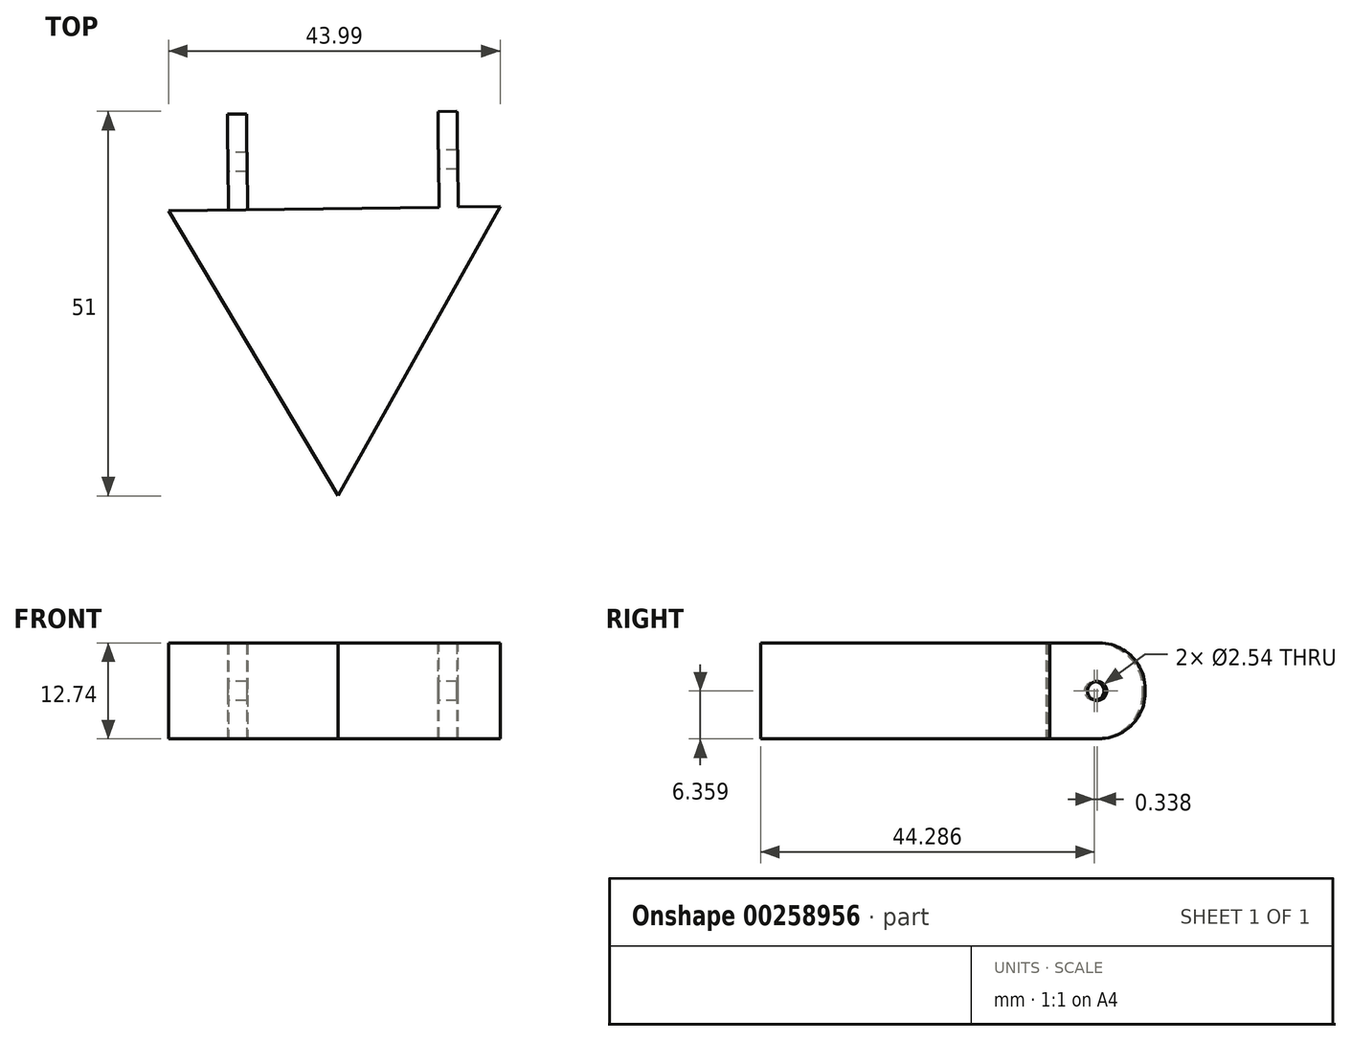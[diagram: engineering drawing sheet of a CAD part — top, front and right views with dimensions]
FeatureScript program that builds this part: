
annotation { "Feature Type Name" : "Feature", "Feature Type Description" : "" }
export const myFeature = defineFeature(function(context is Context, id is Id, definition is map)
    precondition{}
    {
        {
            var Q0;
            Q0=qCreatedBy(makeId("Top.planeOp"),FACE);
            var sketch = newSketch(context, id + "F0", { "sketchPlane" : qUnion([Q0])});
            skCircle(sketch, "E0.cCircle", {"center": v(0, 0) * mm, "radius": 12.7 * mm, "construction": true});
            skLineSegment(sketch, "E0.0", {"start": v(-25, 4.47) * mm, "end": v(16.38, 19.42) * mm});
            skLineSegment(sketch, "E0.1", {"start": v(16.38, 19.42) * mm, "end": v(8.63, -23.9) * mm});
            skLineSegment(sketch, "E0.2", {"start": v(8.63, -23.9) * mm, "end": v(-25, 4.47) * mm});
            skPoint(sketch, "E0.0.midPoint", {"position": v(-4.31, 11.95) * mm});
            skSolve(sketch);
        }
        {
            var Q0;
            Q0=makeQuery(id+"F0.imprint","IMPRINT",FACE,{"disambiguationData":[TD([[makeQuery(id+"F0.imprint","IMPRINT",EDGE,{"derivedFrom":sQuery(id+"F0.wireOp",EDGE,"E0.0")}),-1.0]])]});
            extrude(context, id + "F1", {"entities" : qUnion([Q0]), "depth" : 12.7 * mm});
        }
        {
            var Q0;
            Q0=makeQuery(id+"F1.opExtrude","SWEPT_BODY",BODY,{"disambiguationData":[OSD([sQuery(id+"F0.wireOp",EDGE,"E0.0"),sQuery(id+"F0.wireOp",EDGE,"E0.1"),sQuery(id+"F0.wireOp",EDGE,"E0.2")])]});
            deleteBodies(context, id + "F2", {"entities" : qUnion([Q0])});
        }
        {
            var Q0;
            Q0=qCreatedBy(makeId("Top.planeOp"),FACE);
            var sketch = newSketch(context, id + "F3", { "sketchPlane" : qUnion([Q0])});
            skCircle(sketch, "E1.cCircle", {"center": v(0, 0) * mm, "radius": 12.7 * mm, "construction": true});
            skLineSegment(sketch, "E1.0", {"start": v(21.84, 12.97) * mm, "end": v(0.3, -25.4) * mm});
            skLineSegment(sketch, "E1.1", {"start": v(0.3, -25.4) * mm, "end": v(-22.15, 12.43) * mm});
            skLineSegment(sketch, "E1.2", {"start": v(-22.15, 12.43) * mm, "end": v(21.84, 12.97) * mm});
            skPoint(sketch, "E1.0.midPoint", {"position": v(11.07, -6.22) * mm});
            skSolve(sketch);
        }
        {
            var Q0;
            Q0=makeQuery(id+"F3.imprint","IMPRINT",FACE,{"disambiguationData":[TD([[makeQuery(id+"F3.imprint","IMPRINT",EDGE,{"derivedFrom":sQuery(id+"F3.wireOp",EDGE,"E1.0")}),-1.0]])]});
            extrude(context, id + "F4", {"entities" : qUnion([Q0]), "depth" : 12.7 * mm});
        }
        {
            var Q0;
            Q0=makeQuery(id+"F4.opExtrude","SWEPT_FACE",FACE,{"disambiguationData":[OSD([sQuery(id+"F3.wireOp",EDGE,"E1.2")])]});
            var sketch = newSketch(context, id + "F5", { "sketchPlane" : qUnion([Q0])});
            skLineSegment(sketch, "E2.bottom", {"start": v(-13.88, 0) * mm, "end": v(-16.42, 0) * mm});
            skLineSegment(sketch, "E2.top", {"start": v(-13.88, 12.7) * mm, "end": v(-16.42, 12.7) * mm});
            skLineSegment(sketch, "E2.left", {"start": v(-13.88, 0) * mm, "end": v(-13.88, 12.7) * mm});
            skLineSegment(sketch, "E2.right", {"start": v(-16.42, 0) * mm, "end": v(-16.42, 12.7) * mm});
            skPoint(sketch, "E3.end.orphan", {"position": v(-1.18, 0) * mm});
            skPoint(sketch, "E3.start.orphan", {"position": v(-1.18, 12.7) * mm});
            skPoint(sketch, "E4.orphan", {"position": v(-2.45, 12.7) * mm});
            skPoint(sketch, "E5.top.start.orphan", {"position": v(0.09, 12.7) * mm});
            skPoint(sketch, "E6.orphan", {"position": v(-2.45, 0) * mm});
            skPoint(sketch, "E5.bottom.start.orphan", {"position": v(0.09, 0) * mm});
            skLineSegment(sketch, "E7.bottom", {"start": v(11.52, 12.66) * mm, "end": v(14.06, 12.66) * mm});
            skLineSegment(sketch, "E7.top", {"start": v(11.52, -0.04) * mm, "end": v(14.06, -0.04) * mm});
            skLineSegment(sketch, "E7.left", {"start": v(11.52, 12.66) * mm, "end": v(11.52, -0.04) * mm});
            skLineSegment(sketch, "E7.right", {"start": v(14.06, 12.66) * mm, "end": v(14.06, -0.04) * mm});
            skLineSegment(sketch, "E8", {"start": v(-1.18, 12.7) * mm, "end": v(-1.18, 0) * mm, "construction": true});
            skSolve(sketch);
        }
        {
            var Q0;
            Q0 = qSketchRegion(id + "F5", true);
            extrude(context, id + "F6", {"entities" : qUnion([Q0]), "operationType" : NewBodyOperationType.ADD, "depth" : 12.7 * mm});
        }
        {
            var Q0;
            Q0=makeQuery(id+"F6.opExtrude","SWEPT_FACE",FACE,{"disambiguationData":[OSD([sQuery(id+"F5.wireOp",EDGE,"E7.right")])]});
            var sketch = newSketch(context, id + "F7", { "sketchPlane" : qUnion([Q0])});
            skLineSegment(sketch, "E9", {"start": v(-25.4, 12.66) * mm, "end": v(-12.7, 0) * mm, "construction": true});
            skLineSegment(sketch, "E10", {"start": v(-12.7, 12.66) * mm, "end": v(-25.4, -0.04) * mm, "construction": true});
            skCircle(sketch, "E11", {"center": v(-19.04, 6.32) * mm, "radius": 1.27 * mm});
            skSolve(sketch);
        }
        {
            var Q0;
            Q0=makeQuery(id+"F7.imprint","IMPRINT",FACE,{"disambiguationData":[TD([[makeQuery(id+"F7.imprint","IMPRINT",EDGE,{"derivedFrom":sQuery(id+"F7.wireOp",EDGE,"E11")}),1.0]])]});
            extrude(context, id + "F8", {"entities" : qUnion([Q0]), "operationType" : NewBodyOperationType.REMOVE, "oppositeDirection" : true, "depth" : 41.15 * mm});
        }
        {
            var Q0;
            Q0=makeQuery(id+"F6.opExtrude","CAP_EDGE",EDGE,{"disambiguationData":[OSD([sQuery(id+"F5.wireOp",EDGE,"E7.bottom")])],"isStart":false});
            var Q1;
            Q1=makeQuery(id+"F6.opExtrude","CAP_EDGE",EDGE,{"disambiguationData":[OSD([sQuery(id+"F5.wireOp",EDGE,"E7.top")])],"isStart":false});
            fillet(context, id + "F9", {"entities" : qUnion([Q0, Q1]), "radius" : 6.1 * mm, "tangentPropagation" : true, "allowEdgeOverflow" : false});
        }
        {
            var Q0;
            Q0=makeQuery(id+"F6.opExtrude","CAP_EDGE",EDGE,{"disambiguationData":[OSD([sQuery(id+"F5.wireOp",EDGE,"E2.top")])],"isStart":false});
            var Q1;
            Q1=makeQuery(id+"F6.opExtrude","CAP_EDGE",EDGE,{"disambiguationData":[OSD([sQuery(id+"F5.wireOp",EDGE,"E2.bottom")])],"isStart":false});
            fillet(context, id + "F10", {"entities" : qUnion([Q0, Q1]), "radius" : 6.1 * mm, "tangentPropagation" : true, "allowEdgeOverflow" : false});
        }
    });
